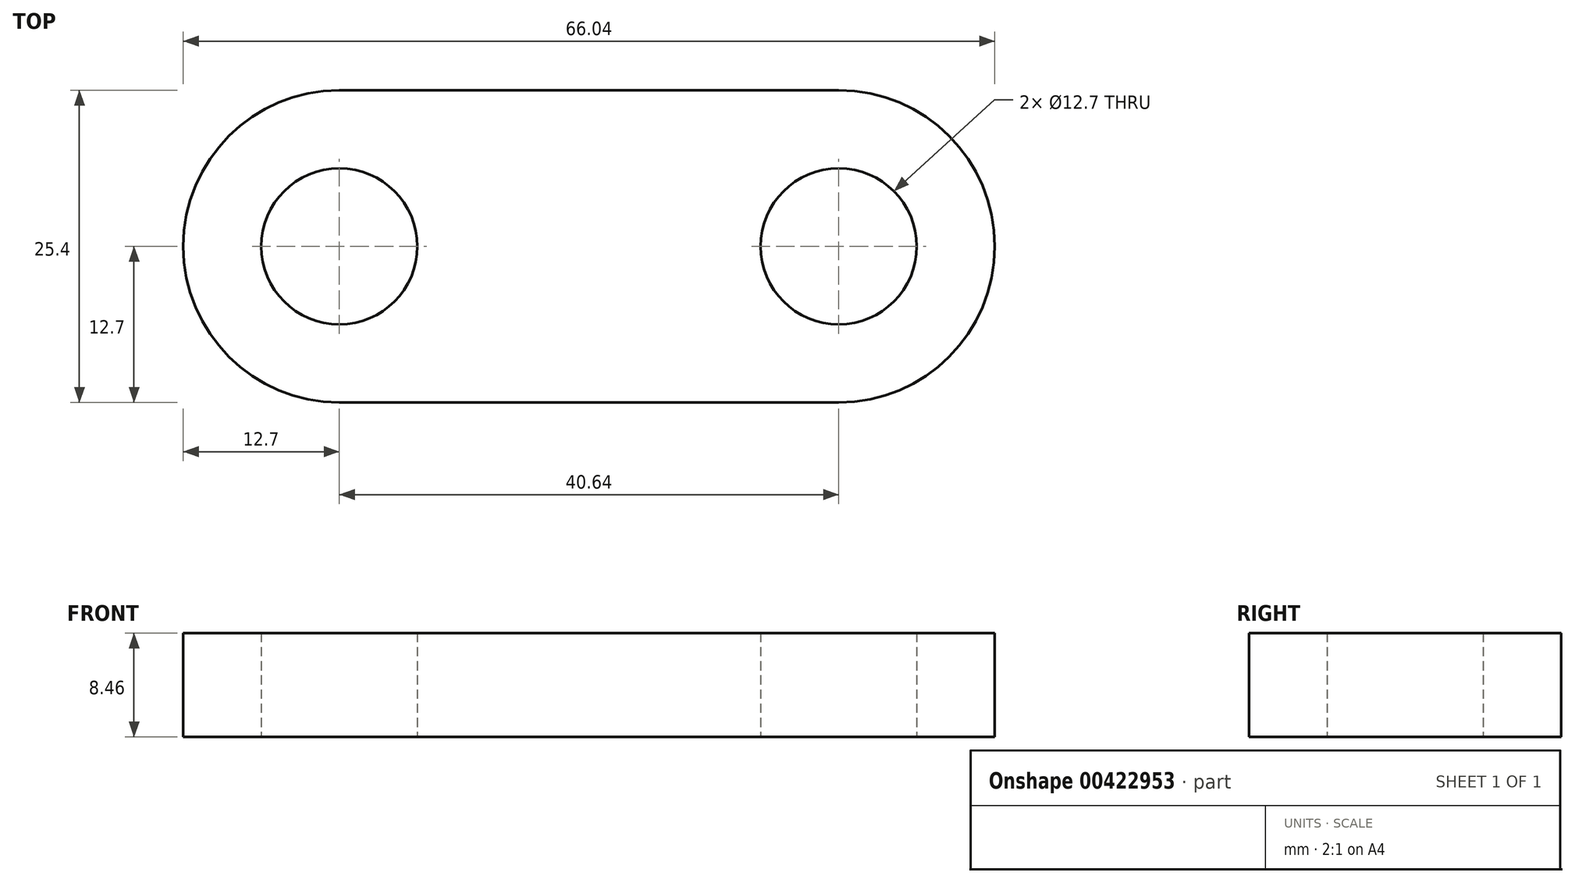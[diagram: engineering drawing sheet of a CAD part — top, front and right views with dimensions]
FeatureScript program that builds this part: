
annotation { "Feature Type Name" : "Feature", "Feature Type Description" : "" }
export const myFeature = defineFeature(function(context is Context, id is Id, definition is map)
    precondition{}
    {
        {
            var Q0;
            Q0=qCreatedBy(makeId("Top.planeOp"),FACE);
            var sketch = newSketch(context, id + "F0", { "sketchPlane" : qUnion([Q0])});
            skCircle(sketch, "E0.MirrorC", {"center": v(0, 0) * mm, "radius": 6.35 * mm});
            skLineSegment(sketch, "E1.MirrorCS", {"start": v(0, 12.7) * mm, "end": v(40.64, 12.7) * mm});
            skLineSegment(sketch, "E2.MirrorCS", {"start": v(0, -12.7) * mm, "end": v(40.64, -12.7) * mm});
            skArc(sketch, "E3", {"start": v(0, 12.7) * mm, "mid": v(-12.7, 0) * mm, "end": v(0, -12.7) * mm});
            skCircle(sketch, "E4", {"center": v(40.64, 0) * mm, "radius": 6.35 * mm});
            skArc(sketch, "E5", {"start": v(40.64, -12.7) * mm, "mid": v(53.34, 0) * mm, "end": v(40.64, 12.7) * mm});
            skSolve(sketch);
        }
        {
            var Q0;
            Q0 = qSketchRegion(id + "F0", true);
            extrude(context, id + "F1", {"entities" : qUnion([Q0]), "depth" : 8.46 * mm, "offsetDistance" : 25.4 * mm});
        }
    });
